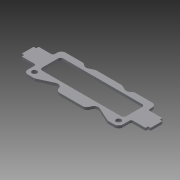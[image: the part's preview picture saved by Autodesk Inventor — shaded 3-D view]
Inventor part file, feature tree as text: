
AUTODESK INVENTOR PART (.ipt)
format: ipt  version: 2015 (Build 190159000, 159)  size: 227,328 bytes
history: native  units: mm
features: extrude x5, sketch x5, fillet x3
ambient origin geometry x8: Origin, YZ Plane, XZ Plane, XY Plane, X Axis, Y Axis, Z Axis, Center Point
bodies: Solid1 (feature_tree)
feature tree (13):
  extrude  "Extrusion1"  Depth=18.0mm
  extrude  "Extrusion3"  Depth=15.0mm
  extrude  "Extrusion6"  Depth=5.0mm
  extrude  "Extrusion7"  Depth=5.0mm
  fillet  "Fillet4"  Radius=113.0mm
  fillet  "Fillet5"  Radius=2.0mm
  fillet  "Fillet6"  Radius=6.0mm
  extrude  "Extrusion8"  Depth=2.0mm
  sketch  "Sketch1"  dims[d11=3.0mm d12=0.0mm d24=18.0mm]
  sketch  "Sketch3"  dims[d25=15.0mm d26=76.5mm]
  sketch  "Sketch4"  dims[d27=3.0mm d28=0.0mm d31=5.0mm]
  sketch  "Sketch7"  dims[d33=5.0mm d36=5.0mm d37=113.0mm d39=2.0mm d40=6.0mm]
  sketch  "Sketch10"  dims[d41=50.0mm d46=2.0mm d48=10.0mm d49=13.0mm d50=3.5mm d54=35.0mm d55=35.0mm d59=3.0mm d60=3.0mm d61=3.0mm d62=3.0mm d64=14.0mm d65=20.0mm d66=3.0mm d67=3.0mm d68=14.0mm d70=3.0mm d71=3.0mm d72=0.0mm d75=2.0mm d76=20.0mm d80=5.0mm d81=30.0mm d82=30.0mm d83=3.0mm d84=0.0mm d85=5.0mm d86=5.0mm d87=5.0mm d88=20.0mm d89=20.0mm d90=25.0mm d91=100.0mm d92=3.0mm d93=3.0mm d94=0.0mm]
